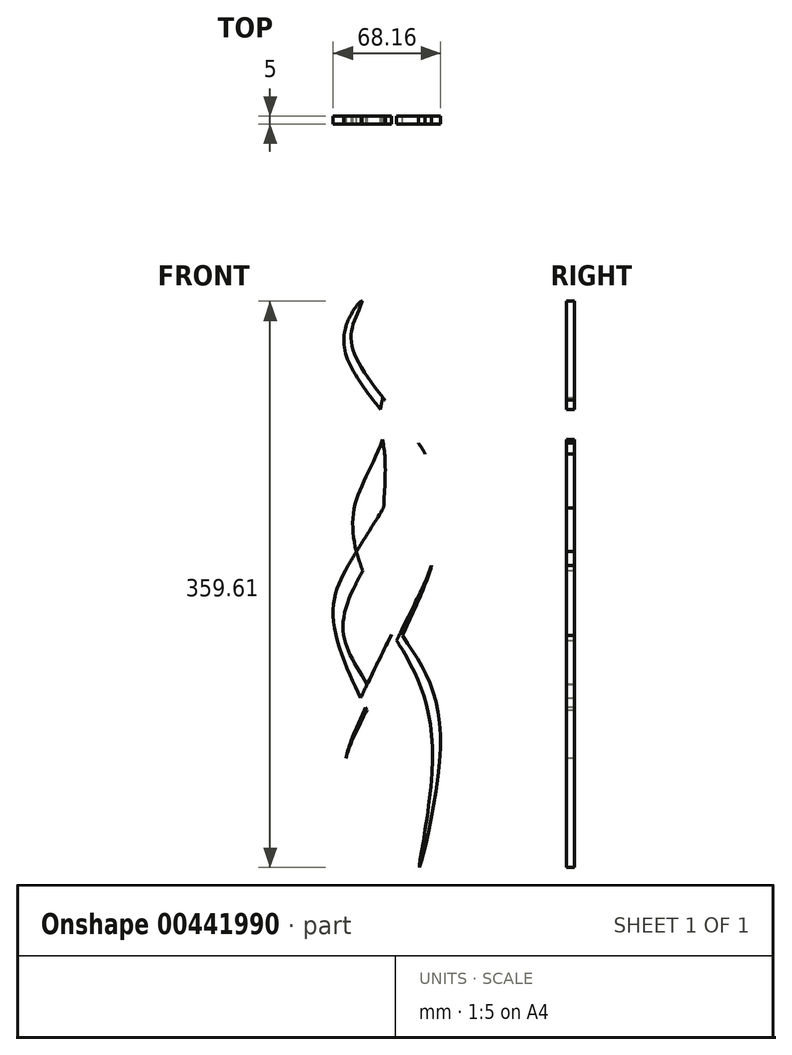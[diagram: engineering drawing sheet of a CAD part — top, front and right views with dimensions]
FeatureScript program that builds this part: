
annotation { "Feature Type Name" : "Feature", "Feature Type Description" : "" }
export const myFeature = defineFeature(function(context is Context, id is Id, definition is map)
    precondition{}
    {
        {
            var Q0;
            Q0=qCreatedBy(makeId("Front.planeOp"),FACE);
            var sketch = newSketch(context, id + "F0", { "sketchPlane" : qUnion([Q0])});
            skLineSegment(sketch, "E0", {"start": v(29.15, 359.6) * mm, "end": v(29.3, 359.6) * mm});
            skLineSegment(sketch, "E1", {"start": v(65.92, 0) * mm, "end": v(65.9, 0) * mm});
            skFitSpline(sketch, "E2", {"points": [v(65.92, 0) * mm, v(79.33, 78.27) * mm, v(60.25, 139.67) * mm, v(31.35, 185.58) * mm, v(25.16, 230.47) * mm, v(48.04, 292.38) * mm, v(45.2, 360) * mm, v(44.73, 317.83) * mm, v(41.27, 291.35) * mm, v(34.97, 268.13) * mm, v(18.46, 229.95) * mm, v(22.07, 187.13) * mm, v(44.77, 153.6) * mm, v(63.86, 121.61) * mm, v(74.18, 63.83) * mm, v(65.92, 0) * mm]});
            skFitSpline(sketch, "E3", {"points": [v(28.78, 0) * mm, v(12.78, 37) * mm, v(17.94, 82.92) * mm, v(50.9, 153.37) * mm, v(71.6, 207.77) * mm, v(62.3, 262.46) * mm, v(17.94, 335.2) * mm, v(29.3, 359.6) * mm, v(25.16, 348.61) * mm, v(24.65, 326.43) * mm, v(57.15, 280.51) * mm, v(75.2, 249.04) * mm, v(76.76, 204.67) * mm, v(60.76, 159.27) * mm, v(30.84, 96.33) * mm, v(17.43, 45.77) * mm, v(28.78, 0) * mm]});
            skFitSpline(sketch, "E4", {"points": [v(48.04, 0) * mm, v(48.04, 82.77) * mm, v(17.43, 153.08) * mm, v(59.21, 235.63) * mm, v(71.08, 306.82) * mm, v(60.23, 360.39) * mm, v(64.89, 322.82) * mm, v(67.47, 280.51) * mm, v(62.3, 262.46) * mm, v(37.55, 219.12) * mm, v(20.46, 191.24) * mm, v(11.23, 159.79) * mm, v(28.73, 107.53) * mm, v(41.27, 71.78) * mm, v(48.04, 0) * mm]});
            skFitSpline(sketch, "E5.trimOffspring", {"points": [v(28.78, 0) * mm, v(12.78, 37) * mm, v(17.94, 82.92) * mm, v(50.89, 153.37) * mm, v(71.6, 207.77) * mm, v(62.3, 262.46) * mm, v(17.94, 335.2) * mm, v(29.3, 359.6) * mm, v(25.16, 348.61) * mm, v(24.65, 326.43) * mm, v(57.15, 280.51) * mm, v(75.2, 249.04) * mm, v(76.76, 204.67) * mm, v(60.76, 159.27) * mm, v(30.84, 96.33) * mm, v(17.43, 45.77) * mm, v(28.78, 0) * mm]});
            skLineSegment(sketch, "E6", {"start": v(44.89, 359.08) * mm, "end": v(44.88, 360) * mm});
            skFitSpline(sketch, "E7", {"points": [v(43.8, 95.2) * mm, v(44.65, 111.26) * mm, v(45.85, 132.07) * mm], "startDerivative": vector(3.04, 30.58) * mm, "endDerivative": vector(-4.93, 21.47) * mm});
            skFitSpline(sketch, "E8", {"points": [v(49.57, 76.18) * mm, v(50.57, 123.66) * mm, v(52.82, 142.05) * mm], "startDerivative": vector(0.63, 86.2) * mm, "endDerivative": vector(6.61, 42.2) * mm});
            skFitSpline(sketch, "E9", {"points": [v(42.09, 166.45) * mm, v(43.83, 192.2) * mm, v(42.02, 207.61) * mm], "startDerivative": vector(5.12, 48.64) * mm, "endDerivative": vector(-5.57, 32.96) * mm});
            skFitSpline(sketch, "E10", {"points": [v(49.2, 155.83) * mm, v(48.11, 191.87) * mm, v(55.01, 228.19) * mm], "startDerivative": vector(-6.03, 72.64) * mm, "endDerivative": vector(17.36, 72.26) * mm});
            skFitSpline(sketch, "E11", {"points": [v(43.18, 228.3) * mm, v(44.23, 256.55) * mm, v(42.6, 271.66) * mm], "startDerivative": vector(3.7, 52.83) * mm, "endDerivative": vector(-5.88, 33.05) * mm});
            skFitSpline(sketch, "E12", {"points": [v(49.66, 239.2) * mm, v(47.62, 262.74) * mm, v(48.18, 282.14) * mm], "startDerivative": vector(-4.58, 45.68) * mm, "endDerivative": vector(2.2, 39.75) * mm});
            skFitSpline(sketch, "E13.trimOffspring", {"points": [v(28.6, 0.64) * mm, v(12.7, 37) * mm, v(17.9, 82.97) * mm, v(50.89, 153.35) * mm, v(71.67, 207.76) * mm, v(62.35, 262.5) * mm, v(17.8, 335.11) * mm, v(29.48, 360.07) * mm, v(25.07, 348.55) * mm, v(24.56, 326.33) * mm, v(57.16, 280.53) * mm, v(75.21, 249.1) * mm, v(77.15, 204.41) * mm, v(59.42, 160.3) * mm, v(29.78, 97.28) * mm, v(18.07, 45.5) * mm, v(28.6, 0.64) * mm]});
            skPoint(sketch, "E14.orphan", {"position": v(0, 0) * mm});
            skLineSegment(sketch, "E15.trimOffspring", {"start": v(28.78, 0) * mm, "end": v(28.69, 0) * mm});
            skLineSegment(sketch, "E16.trimOffspring", {"start": v(48.25, 0) * mm, "end": v(48.04, 0) * mm});
            skPoint(sketch, "E17.end.orphan", {"position": v(96.07, 0) * mm});
            skPoint(sketch, "E18.orphan", {"position": v(77.23, 360.81) * mm});
            skLineSegment(sketch, "E19.trimOffspring", {"start": v(60.22, 360.39) * mm, "end": v(60.23, 360.39) * mm});
            skLineSegment(sketch, "E20.trimOffspring", {"start": v(44.88, 360) * mm, "end": v(45.27, 360) * mm});
            skPoint(sketch, "E21.orphan", {"position": v(12.54, 359.19) * mm});
            skSolve(sketch);
        }
        {
            var Q0;
            {var subQ0=sQuery(id+"F0.wireOp",EDGE,"E3");var subQ1=sQuery(id+"F0.wireOp",EDGE,"E0");var subQ2=makeQuery(id+"F0.imprint","INTERSECT",VERTEX,{"disambiguationData":[OD(0.0)],"derivedFrom":[subQ1,subQ0]});Q0=makeQuery(id+"F0.imprint","IMPRINT",FACE,{"disambiguationData":[TD([[makeQuery(id+"F0.imprint","IMPRINT",EDGE,{"disambiguationData":[TD([[subQ2,-1.0]])],"derivedFrom":subQ1}),-1.0]])]});}
            var Q1;
            {var subQ0=sQuery(id+"F0.wireOp",EDGE,"E2");var subQ1=sQuery(id+"F0.wireOp",EDGE,"E0");var subQ2=makeQuery(id+"F0.imprint","INTERSECT",VERTEX,{"disambiguationData":[OD(0.0)],"derivedFrom":[subQ1,subQ0]});Q1=makeQuery(id+"F0.imprint","IMPRINT",FACE,{"disambiguationData":[TD([[makeQuery(id+"F0.imprint","IMPRINT",EDGE,{"disambiguationData":[TD([[subQ2,-1.0]])],"derivedFrom":subQ1}),-1.0]])]});}
            var Q2;
            {var subQ0=sQuery(id+"F0.wireOp",EDGE,"E4");var subQ1=sQuery(id+"F0.wireOp",EDGE,"E3");var subQ2=makeQuery(id+"F0.imprint","INTERSECT",VERTEX,{"disambiguationData":[OD(4.0)],"derivedFrom":[subQ1,subQ0]});Q2=makeQuery(id+"F0.imprint","IMPRINT",FACE,{"disambiguationData":[TD([[makeQuery(id+"F0.imprint","IMPRINT",EDGE,{"disambiguationData":[TD([[subQ2,-1.0]])],"derivedFrom":subQ1}),1.0]])]});}
            var Q3;
            {var subQ0=sQuery(id+"F0.wireOp",EDGE,"E3");var subQ1=sQuery(id+"F0.wireOp",EDGE,"E2");var subQ2=makeQuery(id+"F0.imprint","INTERSECT",VERTEX,{"disambiguationData":[OD(2.0)],"derivedFrom":[subQ1,subQ0]});Q3=makeQuery(id+"F0.imprint","IMPRINT",FACE,{"disambiguationData":[TD([[makeQuery(id+"F0.imprint","IMPRINT",EDGE,{"disambiguationData":[TD([[subQ2,-1.0]])],"derivedFrom":subQ1}),1.0]])]});}
            var Q4;
            {var subQ0=sQuery(id+"F0.wireOp",EDGE,"E3");var subQ1=sQuery(id+"F0.wireOp",EDGE,"E2");var subQ2=makeQuery(id+"F0.imprint","INTERSECT",VERTEX,{"disambiguationData":[OD(2.0)],"derivedFrom":[subQ1,subQ0]});Q4=makeQuery(id+"F0.imprint","IMPRINT",FACE,{"disambiguationData":[TD([[makeQuery(id+"F0.imprint","IMPRINT",EDGE,{"disambiguationData":[TD([[subQ2,-1.0]])],"derivedFrom":subQ1}),-1.0]])]});}
            var Q5;
            {var subQ0=sQuery(id+"F0.wireOp",EDGE,"E4");var subQ1=sQuery(id+"F0.wireOp",EDGE,"E3");var subQ2=makeQuery(id+"F0.imprint","INTERSECT",VERTEX,{"disambiguationData":[OD(2.0)],"derivedFrom":[subQ1,subQ0]});Q5=makeQuery(id+"F0.imprint","IMPRINT",FACE,{"disambiguationData":[TD([[makeQuery(id+"F0.imprint","IMPRINT",EDGE,{"disambiguationData":[TD([[subQ2,-1.0]])],"derivedFrom":subQ1}),-1.0]])]});}
            var Q6;
            {var subQ0=sQuery(id+"F0.wireOp",EDGE,"E4");var subQ1=sQuery(id+"F0.wireOp",EDGE,"E2");var subQ2=makeQuery(id+"F0.imprint","INTERSECT",VERTEX,{"disambiguationData":[OD(1.0)],"derivedFrom":[subQ1,subQ0]});Q6=makeQuery(id+"F0.imprint","IMPRINT",FACE,{"disambiguationData":[TD([[makeQuery(id+"F0.imprint","IMPRINT",EDGE,{"disambiguationData":[TD([[subQ2,-1.0]])],"derivedFrom":subQ1}),1.0]])]});}
            var Q7;
            {var subQ0=sQuery(id+"F0.wireOp",EDGE,"E4");var subQ1=sQuery(id+"F0.wireOp",EDGE,"E2");var subQ2=makeQuery(id+"F0.imprint","INTERSECT",VERTEX,{"disambiguationData":[OD(0.0)],"derivedFrom":[subQ1,subQ0]});Q7=makeQuery(id+"F0.imprint","IMPRINT",FACE,{"disambiguationData":[TD([[makeQuery(id+"F0.imprint","IMPRINT",EDGE,{"disambiguationData":[TD([[subQ2,-1.0]])],"derivedFrom":subQ1}),-1.0]])]});}
            var Q8;
            {var subQ0=sQuery(id+"F0.wireOp",EDGE,"E3");var subQ1=sQuery(id+"F0.wireOp",EDGE,"E2");var subQ2=makeQuery(id+"F0.imprint","INTERSECT",VERTEX,{"disambiguationData":[OD(0.0)],"derivedFrom":[subQ1,subQ0]});Q8=makeQuery(id+"F0.imprint","IMPRINT",FACE,{"disambiguationData":[TD([[makeQuery(id+"F0.imprint","IMPRINT",EDGE,{"disambiguationData":[TD([[subQ2,-1.0]])],"derivedFrom":subQ1}),-1.0]])]});}
            var Q9;
            {var subQ0=sQuery(id+"F0.wireOp",EDGE,"E4");var subQ1=sQuery(id+"F0.wireOp",EDGE,"E2");var subQ2=makeQuery(id+"F0.imprint","INTERSECT",VERTEX,{"disambiguationData":[OD(0.0)],"derivedFrom":[subQ1,subQ0]});Q9=makeQuery(id+"F0.imprint","IMPRINT",FACE,{"disambiguationData":[TD([[makeQuery(id+"F0.imprint","IMPRINT",EDGE,{"disambiguationData":[TD([[subQ2,-1.0]])],"derivedFrom":subQ1}),1.0]])]});}
            var Q10;
            {var subQ0=sQuery(id+"F0.wireOp",EDGE,"E4");var subQ1=sQuery(id+"F0.wireOp",EDGE,"E2");var subQ2=makeQuery(id+"F0.imprint","INTERSECT",VERTEX,{"disambiguationData":[OD(2.0)],"derivedFrom":[subQ1,subQ0]});Q10=makeQuery(id+"F0.imprint","IMPRINT",FACE,{"disambiguationData":[TD([[makeQuery(id+"F0.imprint","IMPRINT",EDGE,{"disambiguationData":[TD([[subQ2,-1.0]])],"derivedFrom":subQ1}),-1.0]])]});}
            var Q11;
            {var subQ0=sQuery(id+"F0.wireOp",EDGE,"E3");var subQ1=sQuery(id+"F0.wireOp",EDGE,"E2");var subQ2=makeQuery(id+"F0.imprint","INTERSECT",VERTEX,{"disambiguationData":[OD(1.0)],"derivedFrom":[subQ1,subQ0]});Q11=makeQuery(id+"F0.imprint","IMPRINT",FACE,{"disambiguationData":[TD([[makeQuery(id+"F0.imprint","IMPRINT",EDGE,{"disambiguationData":[TD([[subQ2,-1.0]])],"derivedFrom":subQ1}),1.0]])]});}
            var Q12;
            {var subQ0=sQuery(id+"F0.wireOp",EDGE,"E2");var subQ1=sQuery(id+"F0.wireOp",EDGE,"E1");var subQ2=makeQuery(id+"F0.imprint","INTERSECT",VERTEX,{"disambiguationData":[OD(0.0)],"derivedFrom":[subQ1,subQ0]});Q12=makeQuery(id+"F0.imprint","IMPRINT",FACE,{"disambiguationData":[TD([[makeQuery(id+"F0.imprint","IMPRINT",EDGE,{"disambiguationData":[TD([[subQ2,-1.0]])],"derivedFrom":subQ1}),-1.0]])]});}
            var Q13;
            {var subQ0=sQuery(id+"F0.wireOp",EDGE,"E3");var subQ1=sQuery(id+"F0.wireOp",EDGE,"E2");var subQ2=makeQuery(id+"F0.imprint","INTERSECT",VERTEX,{"disambiguationData":[OD(6.0)],"derivedFrom":[subQ1,subQ0]});Q13=makeQuery(id+"F0.imprint","IMPRINT",FACE,{"disambiguationData":[TD([[makeQuery(id+"F0.imprint","IMPRINT",EDGE,{"disambiguationData":[TD([[subQ2,-1.0]])],"derivedFrom":subQ1}),-1.0]])]});}
            var Q14;
            {var subQ0=sQuery(id+"F0.wireOp",EDGE,"E3");var subQ1=sQuery(id+"F0.wireOp",EDGE,"E2");var subQ2=makeQuery(id+"F0.imprint","INTERSECT",VERTEX,{"disambiguationData":[OD(0.0)],"derivedFrom":[subQ1,subQ0]});Q14=makeQuery(id+"F0.imprint","IMPRINT",FACE,{"disambiguationData":[TD([[makeQuery(id+"F0.imprint","IMPRINT",EDGE,{"disambiguationData":[TD([[subQ2,-1.0]])],"derivedFrom":subQ1}),1.0]])]});}
            var Q15;
            {var subQ0=sQuery(id+"F0.wireOp",EDGE,"E3");var subQ1=sQuery(id+"F0.wireOp",EDGE,"E1");var subQ2=makeQuery(id+"F0.imprint","INTERSECT",VERTEX,{"disambiguationData":[OD(0.0)],"derivedFrom":[subQ1,subQ0]});Q15=makeQuery(id+"F0.imprint","IMPRINT",FACE,{"disambiguationData":[TD([[makeQuery(id+"F0.imprint","IMPRINT",EDGE,{"disambiguationData":[TD([[subQ2,-1.0]])],"derivedFrom":subQ1}),-1.0]])]});}
            var Q16;
            {var subQ0=sQuery(id+"F0.wireOp",EDGE,"E4");var subQ1=sQuery(id+"F0.wireOp",EDGE,"E1");var subQ2=makeQuery(id+"F0.imprint","INTERSECT",VERTEX,{"disambiguationData":[OD(0.0)],"derivedFrom":[subQ1,subQ0]});Q16=makeQuery(id+"F0.imprint","IMPRINT",FACE,{"disambiguationData":[TD([[makeQuery(id+"F0.imprint","IMPRINT",EDGE,{"disambiguationData":[TD([[subQ2,-1.0]])],"derivedFrom":subQ1}),-1.0]])]});}
            var Q17;
            {var subQ0=sQuery(id+"F0.wireOp",EDGE,"E4");var subQ1=sQuery(id+"F0.wireOp",EDGE,"E3");var subQ2=makeQuery(id+"F0.imprint","INTERSECT",VERTEX,{"disambiguationData":[OD(0.0)],"derivedFrom":[subQ1,subQ0]});Q17=makeQuery(id+"F0.imprint","IMPRINT",FACE,{"disambiguationData":[TD([[makeQuery(id+"F0.imprint","IMPRINT",EDGE,{"disambiguationData":[TD([[subQ2,-1.0]])],"derivedFrom":subQ1}),-1.0]])]});}
            extrude(context, id + "F1", {"entities" : qUnion([Q0, Q1, Q2, Q3, Q4, Q5, Q6, Q7, Q8, Q9, Q10, Q11, Q12, Q13, Q14, Q15, Q16, Q17]), "depth" : 5 * mm});
        }
    });
